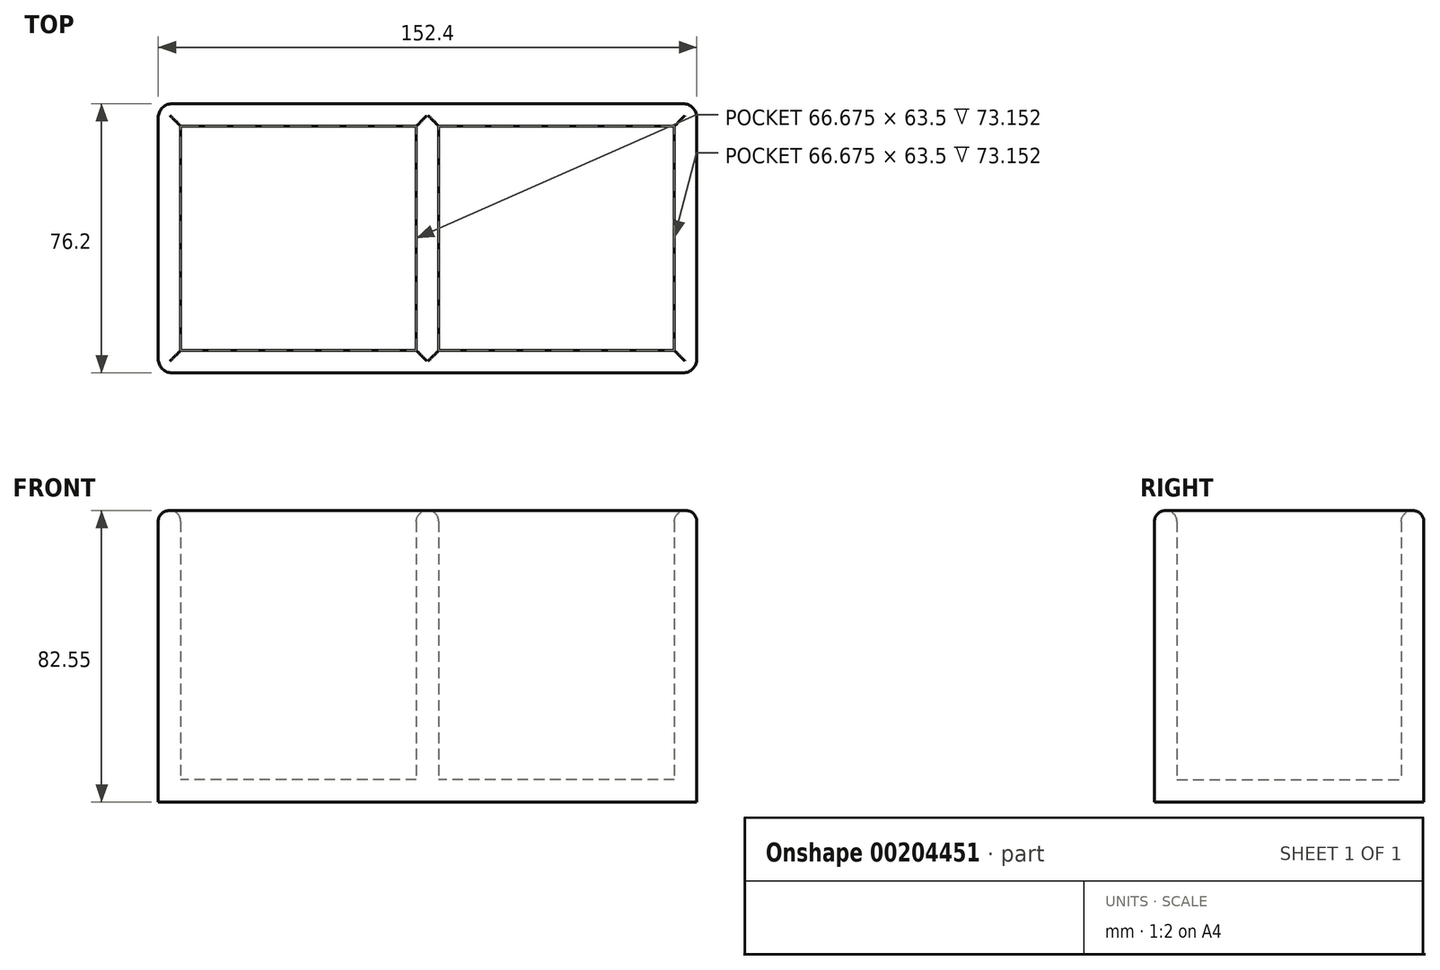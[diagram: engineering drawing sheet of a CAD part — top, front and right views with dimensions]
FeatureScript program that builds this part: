
annotation { "Feature Type Name" : "Feature", "Feature Type Description" : "" }
export const myFeature = defineFeature(function(context is Context, id is Id, definition is map)
    precondition{}
    {
        {
            var Q0;
            Q0=qCreatedBy(makeId("Top.planeOp"),FACE);
            var sketch = newSketch(context, id + "F0", { "sketchPlane" : qUnion([Q0])});
            skLineSegment(sketch, "E0", {"start": v(-196.08, -53.24) * mm, "end": v(-43.68, -53.24) * mm});
            skLineSegment(sketch, "E1", {"start": v(-43.68, -53.24) * mm, "end": v(-43.68, 22.96) * mm});
            skLineSegment(sketch, "E2", {"start": v(-43.68, 22.96) * mm, "end": v(-196.08, 22.96) * mm});
            skLineSegment(sketch, "E3", {"start": v(-196.08, 22.96) * mm, "end": v(-196.08, -53.24) * mm});
            skSolve(sketch);
        }
        {
            var Q0;
            Q0=makeQuery(id+"F0.imprint","IMPRINT",FACE,{"disambiguationData":[TD([[makeQuery(id+"F0.imprint","IMPRINT",EDGE,{"derivedFrom":sQuery(id+"F0.wireOp",EDGE,"E0")}),1.0]])]});
            extrude(context, id + "F1", {"entities" : qUnion([Q0]), "depth" : 6.35 * mm});
        }
        {
            var Q0;
            Q0=makeQuery(id+"F1.opExtrude","CAP_FACE",FACE,{"disambiguationData":[OSD([sQuery(id+"F0.wireOp",EDGE,"E0"),sQuery(id+"F0.wireOp",EDGE,"E1"),sQuery(id+"F0.wireOp",EDGE,"E2"),sQuery(id+"F0.wireOp",EDGE,"E3")])],"isStart":false});
            var sketch = newSketch(context, id + "F2", { "sketchPlane" : qUnion([Q0])});
            skLineSegment(sketch, "E4", {"start": v(-196.08, 22.96) * mm, "end": v(-196.08, -53.24) * mm});
            skLineSegment(sketch, "E5", {"start": v(-43.68, 22.96) * mm, "end": v(-43.68, -53.24) * mm});
            skLineSegment(sketch, "E6.0", {"start": v(-189.73, 16.6) * mm, "end": v(-189.73, -46.9) * mm});
            skLineSegment(sketch, "E6.1", {"start": v(-50.03, 16.6) * mm, "end": v(-116.7, 16.6) * mm});
            skLineSegment(sketch, "E6.2", {"start": v(-50.03, -46.9) * mm, "end": v(-50.03, 16.6) * mm});
            skLineSegment(sketch, "E6.3", {"start": v(-189.73, -46.9) * mm, "end": v(-123.05, -46.9) * mm});
            skLineSegment(sketch, "E7", {"start": v(-116.7, -46.9) * mm, "end": v(-116.7, 16.6) * mm});
            skLineSegment(sketch, "E8", {"start": v(-123.05, -46.9) * mm, "end": v(-123.05, 16.6) * mm});
            skLineSegment(sketch, "E9.trimOffspring", {"start": v(-123.05, 16.6) * mm, "end": v(-189.73, 16.6) * mm});
            skLineSegment(sketch, "E10.trimOffspring", {"start": v(-116.7, -46.9) * mm, "end": v(-50.03, -46.9) * mm});
            skSolve(sketch);
        }
        {
            var Q0;
            Q0=makeQuery(id+"F2.imprint","IMPRINT",FACE,{"disambiguationData":[TD([[makeQuery(id+"F2.imprint","IMPRINT",EDGE,{"derivedFrom":sQuery(id+"F2.wireOp",EDGE,"E4")}),1.0]])]});
            extrude(context, id + "F3", {"entities" : qUnion([Q0]), "operationType" : NewBodyOperationType.ADD, "depth" : 76.2 * mm});
        }
        {
            var Q0;
            Q0=makeQuery(id+"F3.opExtrude","CAP_EDGE",EDGE,{"disambiguationData":[OSD([sQuery(id+"F2.wireOp",EDGE,"E4")])],"isStart":false});
            var Q1;
            Q1=makeQuery(id+"F3.opExtrude","CAP_EDGE",EDGE,{"disambiguationData":[OSD([sQuery(id+"F0.wireOp",EDGE,"E2")])],"isStart":false});
            var Q2;
            Q2=makeQuery(id+"F3.opExtrude","CAP_EDGE",EDGE,{"disambiguationData":[OSD([sQuery(id+"F2.wireOp",EDGE,"E5")])],"isStart":false});
            var Q3;
            Q3=makeQuery(id+"F3.opExtrude","CAP_EDGE",EDGE,{"disambiguationData":[OSD([sQuery(id+"F0.wireOp",EDGE,"E0")])],"isStart":false});
            var Q4;
            Q4=makeQuery(id+"F3.opExtrude","CAP_EDGE",EDGE,{"disambiguationData":[OSD([sQuery(id+"F2.wireOp",EDGE,"3e1e0603-1fb5-4972-9baa-8bbe23365f9b.trimOffspring")])],"isStart":false});
            var Q5;
            Q5=makeQuery(id+"F3.opExtrude","CAP_EDGE",EDGE,{"disambiguationData":[OSD([sQuery(id+"F2.wireOp",EDGE,"1c034980-66c7-4a99-88f6-809af28da6af.2")])],"isStart":false});
            var Q6;
            Q6=makeQuery(id+"F3.opExtrude","CAP_EDGE",EDGE,{"disambiguationData":[OSD([sQuery(id+"F2.wireOp",EDGE,"34jvmDVA-LBMt-WicD-udHb-h8wt2wgJGJPJ")])],"isStart":false});
            var Q7;
            Q7=makeQuery(id+"F3.opExtrude","CAP_EDGE",EDGE,{"disambiguationData":[OSD([sQuery(id+"F2.wireOp",EDGE,"5586644b-fcf1-4768-81e4-0579790f2cb7.trimOffspring")])],"isStart":false});
            var Q8;
            Q8=makeQuery(id+"F3.opExtrude","CAP_EDGE",EDGE,{"disambiguationData":[OSD([sQuery(id+"F2.wireOp",EDGE,"f7efb799-9370-4bb4-8484-d8ee514120ca.trimOffspring")])],"isStart":false});
            var Q9;
            Q9=makeQuery(id+"F3.opExtrude","CAP_EDGE",EDGE,{"disambiguationData":[OSD([sQuery(id+"F2.wireOp",EDGE,"99c2d68a-9c83-4ae3-961a-4b3d6f359155.trimOffspring")])],"isStart":false});
            var Q10;
            Q10=makeQuery(id+"F3.opExtrude","CAP_EDGE",EDGE,{"disambiguationData":[OSD([sQuery(id+"F2.wireOp",EDGE,"2e39c922-4422-408e-88a4-50d7e34ec590.trimOffspring")])],"isStart":false});
            var Q11;
            Q11=makeQuery(id+"F3.opExtrude","CAP_EDGE",EDGE,{"disambiguationData":[OSD([sQuery(id+"F2.wireOp",EDGE,"VM4zdoIK-6OeH-8iNt-Jz0q-MQBKBw6Ai8jk")])],"isStart":false});
            var Q12;
            Q12=makeQuery(id+"F3.opExtrude","CAP_EDGE",EDGE,{"disambiguationData":[OSD([sQuery(id+"F2.wireOp",EDGE,"cead821d-81f0-4ad0-aa16-42e17c700e5e.trimOffspring")])],"isStart":false});
            var Q13;
            Q13=makeQuery(id+"F3.opExtrude","CAP_EDGE",EDGE,{"disambiguationData":[OSD([sQuery(id+"F2.wireOp",EDGE,"4a7d65c7-206e-4f51-a3b6-8e69b7e0af4c.trimOffspring")])],"isStart":false});
            var Q14;
            Q14=makeQuery(id+"F3.opExtrude","CAP_EDGE",EDGE,{"disambiguationData":[OSD([sQuery(id+"F2.wireOp",EDGE,"1c034980-66c7-4a99-88f6-809af28da6af.0")])],"isStart":false});
            var Q15;
            Q15=makeQuery(id+"F3.opExtrude","CAP_EDGE",EDGE,{"disambiguationData":[OSD([sQuery(id+"F2.wireOp",EDGE,"35b4b2be-cfb8-4c57-a2d5-533fb1d1daa8.trimOffspring")])],"isStart":false});
            var Q16;
            Q16=makeQuery(id+"F3.opExtrude","CAP_EDGE",EDGE,{"disambiguationData":[OSD([sQuery(id+"F2.wireOp",EDGE,"80beca5c-7ea5-45bb-8854-6afced174f42.trimOffspring")])],"isStart":false});
            var Q17;
            Q17=makeQuery(id+"F3.opExtrude","CAP_EDGE",EDGE,{"disambiguationData":[OSD([sQuery(id+"F2.wireOp",EDGE,"1c034980-66c7-4a99-88f6-809af28da6af.1")])],"isStart":false});
            var Q18;
            Q18=makeQuery(id+"F3.opExtrude","CAP_EDGE",EDGE,{"disambiguationData":[OSD([sQuery(id+"F2.wireOp",EDGE,"fe041d47-b4e4-45e7-a19a-2848fcd3202c.trimOffspring")])],"isStart":false});
            var Q19;
            Q19=makeQuery(id+"F3.opExtrude","CAP_EDGE",EDGE,{"disambiguationData":[OSD([sQuery(id+"F2.wireOp",EDGE,"z9YfiH5v-LgKR-as8u-naAg-T7Y7hvb0q66K")])],"isStart":false});
            var Q20;
            Q20=makeQuery(id+"F3.opExtrude","CAP_EDGE",EDGE,{"disambiguationData":[OSD([sQuery(id+"F2.wireOp",EDGE,"qIHNaSYz-l4Lo-Q6WJ-0X88-zKGYzDomG7mt")])],"isStart":false});
            var Q21;
            Q21=makeQuery(id+"F3.opExtrude","CAP_EDGE",EDGE,{"disambiguationData":[OSD([sQuery(id+"F2.wireOp",EDGE,"8Xfg7Xhl-s1w8-5y9W-gDjH-7PRa0HVQ9ZBo")])],"isStart":false});
            var Q22;
            Q22=makeQuery(id+"F3.opExtrude","CAP_EDGE",EDGE,{"disambiguationData":[OSD([sQuery(id+"F2.wireOp",EDGE,"044ab6cf-a9b9-4fd2-bb40-7f8ee2d51c71.trimOffspring")])],"isStart":false});
            var Q23;
            Q23=makeQuery(id+"F3.opExtrude","CAP_EDGE",EDGE,{"disambiguationData":[OSD([sQuery(id+"F2.wireOp",EDGE,"d7598cd1-cb8d-413c-b2cf-3a15344e7c9d.trimOffspring")])],"isStart":false});
            var Q24;
            Q24=makeQuery(id+"F3.opExtrude","CAP_FACE",FACE,{"disambiguationData":[OSD([sQuery(id+"F0.wireOp",EDGE,"E0"),sQuery(id+"F0.wireOp",EDGE,"E2"),sQuery(id+"F2.wireOp",EDGE,"E4"),sQuery(id+"F2.wireOp",EDGE,"E5"),sQuery(id+"F2.wireOp",EDGE,"1c034980-66c7-4a99-88f6-809af28da6af.0"),sQuery(id+"F2.wireOp",EDGE,"1c034980-66c7-4a99-88f6-809af28da6af.1"),sQuery(id+"F2.wireOp",EDGE,"1c034980-66c7-4a99-88f6-809af28da6af.2"),sQuery(id+"F2.wireOp",EDGE,"1c034980-66c7-4a99-88f6-809af28da6af.3"),sQuery(id+"F2.wireOp",EDGE,"NjVL9rNB-uVnU-LTqP-3PAM-pbAwrqNA0hr7"),sQuery(id+"F2.wireOp",EDGE,"qIHNaSYz-l4Lo-Q6WJ-0X88-zKGYzDomG7mt"),sQuery(id+"F2.wireOp",EDGE,"QIcNDbXF-uMSr-SeDP-0Iz7-MjdTmpDnTODz"),sQuery(id+"F2.wireOp",EDGE,"z9YfiH5v-LgKR-as8u-naAg-T7Y7hvb0q66K"),sQuery(id+"F2.wireOp",EDGE,"8Xfg7Xhl-s1w8-5y9W-gDjH-7PRa0HVQ9ZBo"),sQuery(id+"F2.wireOp",EDGE,"VM4zdoIK-6OeH-8iNt-Jz0q-MQBKBw6Ai8jk"),sQuery(id+"F2.wireOp",EDGE,"35b4b2be-cfb8-4c57-a2d5-533fb1d1daa8.trimOffspring"),sQuery(id+"F2.wireOp",EDGE,"80beca5c-7ea5-45bb-8854-6afced174f42.trimOffspring"),sQuery(id+"F2.wireOp",EDGE,"4a7d65c7-206e-4f51-a3b6-8e69b7e0af4c.trimOffspring"),sQuery(id+"F2.wireOp",EDGE,"34jvmDVA-LBMt-WicD-udHb-h8wt2wgJGJPJ"),sQuery(id+"F2.wireOp",EDGE,"fe041d47-b4e4-45e7-a19a-2848fcd3202c.trimOffspring"),sQuery(id+"F2.wireOp",EDGE,"d7598cd1-cb8d-413c-b2cf-3a15344e7c9d.trimOffspring"),sQuery(id+"F2.wireOp",EDGE,"5586644b-fcf1-4768-81e4-0579790f2cb7.trimOffspring"),sQuery(id+"F2.wireOp",EDGE,"f7efb799-9370-4bb4-8484-d8ee514120ca.trimOffspring"),sQuery(id+"F2.wireOp",EDGE,"3e1e0603-1fb5-4972-9baa-8bbe23365f9b.trimOffspring"),sQuery(id+"F2.wireOp",EDGE,"04753417-8eac-4215-9838-a12e24f76e92.trimOffspring"),sQuery(id+"F2.wireOp",EDGE,"cead821d-81f0-4ad0-aa16-42e17c700e5e.trimOffspring"),sQuery(id+"F2.wireOp",EDGE,"044ab6cf-a9b9-4fd2-bb40-7f8ee2d51c71.trimOffspring"),sQuery(id+"F2.wireOp",EDGE,"99c2d68a-9c83-4ae3-961a-4b3d6f359155.trimOffspring"),sQuery(id+"F2.wireOp",EDGE,"2e39c922-4422-408e-88a4-50d7e34ec590.trimOffspring")])],"isStart":false});
            fillet(context, id + "F4", {"entities" : qUnion([Q0, Q1, Q2, Q3, Q4, Q5, Q6, Q7, Q8, Q9, Q10, Q11, Q12, Q13, Q14, Q15, Q16, Q17, Q18, Q19, Q20, Q21, Q22, Q23, Q24]), "radius" : 3.05 * mm, "tangentPropagation" : true, "allowEdgeOverflow" : false});
        }
        {
            var Q0;
            Q0=makeQuery(id+"F3.boolean.opBoolean","MERGE",EDGE,{"derivedFrom":[makeQuery(id+"F1.opExtrude","SWEPT_EDGE",EDGE,{"disambiguationData":[OSD([sQuery(id+"F0.wireOp",EDGE,"E0"),sQuery(id+"F0.wireOp",EDGE,"E1")])]}),makeQuery(id+"F3.opExtrude","SWEPT_EDGE",EDGE,{"disambiguationData":[OSD([sQuery(id+"F2.wireOp",EDGE,"E5"),sQuery(id+"F2.wireOp",EDGE,"oCvONeEV-RT9G-SCc4-ZoTs-1H44UNEZmW0B")])]})]});
            var Q1;
            Q1=makeQuery(id+"F3.boolean.opBoolean","MERGE",EDGE,{"derivedFrom":[makeQuery(id+"F1.opExtrude","SWEPT_EDGE",EDGE,{"disambiguationData":[OSD([sQuery(id+"F0.wireOp",EDGE,"E1"),sQuery(id+"F0.wireOp",EDGE,"E2")])]}),makeQuery(id+"F3.opExtrude","SWEPT_EDGE",EDGE,{"disambiguationData":[OSD([sQuery(id+"F2.wireOp",EDGE,"br9ruojc-25v7-t9U2-Ebwy-x7YlbIF3SD61"),sQuery(id+"F2.wireOp",EDGE,"E5")])]})]});
            var Q2;
            Q2=makeQuery(id+"F3.boolean.opBoolean","MERGE",EDGE,{"derivedFrom":[makeQuery(id+"F1.opExtrude","SWEPT_EDGE",EDGE,{"disambiguationData":[OSD([sQuery(id+"F0.wireOp",EDGE,"E0"),sQuery(id+"F0.wireOp",EDGE,"E3")])]}),makeQuery(id+"F3.opExtrude","SWEPT_EDGE",EDGE,{"disambiguationData":[OSD([sQuery(id+"F2.wireOp",EDGE,"E4"),sQuery(id+"F2.wireOp",EDGE,"bB0LzwJd-MyAT-vHgI-KBgQ-vy4sWA4kjwKj")])]})]});
            var Q3;
            Q3=makeQuery(id+"F3.boolean.opBoolean","MERGE",EDGE,{"derivedFrom":[makeQuery(id+"F1.opExtrude","SWEPT_EDGE",EDGE,{"disambiguationData":[OSD([sQuery(id+"F0.wireOp",EDGE,"E2"),sQuery(id+"F0.wireOp",EDGE,"E3")])]}),makeQuery(id+"F3.opExtrude","SWEPT_EDGE",EDGE,{"disambiguationData":[OSD([sQuery(id+"F2.wireOp",EDGE,"mnQSM7e8-kL0t-ZU6Y-u3rO-901lSrKtSyTH"),sQuery(id+"F2.wireOp",EDGE,"E4")])]})]});
            fillet(context, id + "F5", {"entities" : qUnion([Q0, Q1, Q2, Q3]), "radius" : 3.91 * mm, "tangentPropagation" : true, "allowEdgeOverflow" : false});
        }
    });
